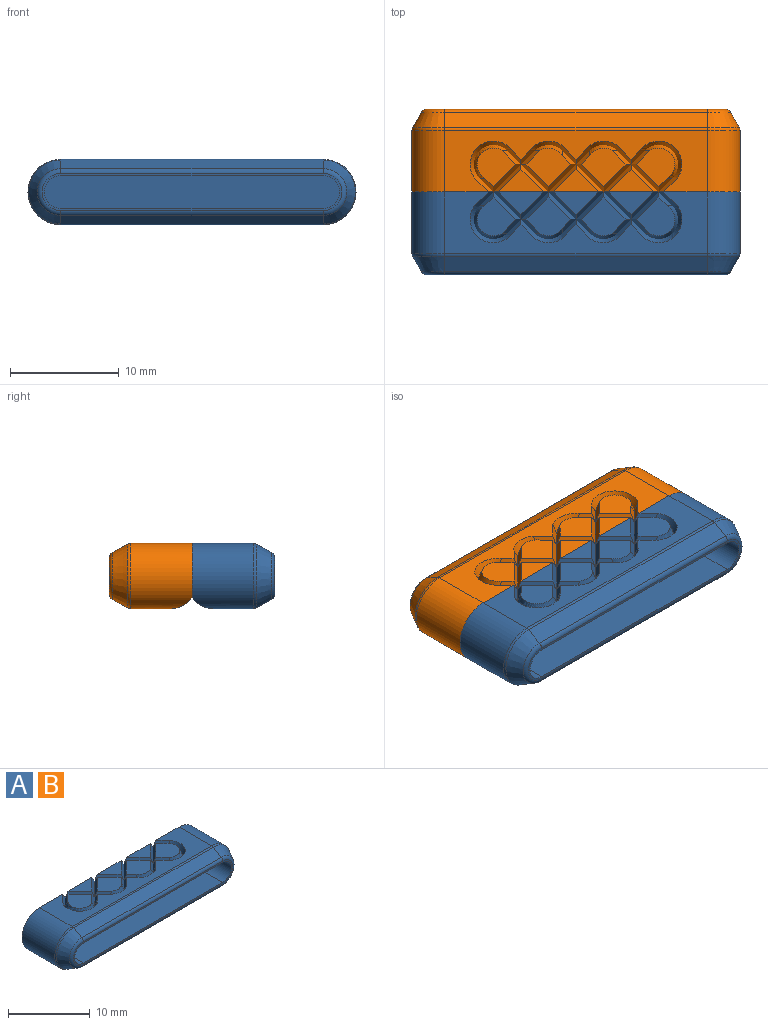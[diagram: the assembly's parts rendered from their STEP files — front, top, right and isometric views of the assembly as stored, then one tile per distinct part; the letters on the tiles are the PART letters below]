
ASSEMBLY  parts=2 mates=1
PART A: 75 faces, bbox 30.7x7.7x6.6 mm
  f0: plane 24.15x3.66mm, normal (0,0,-1), area 88.4mm2, adj f2,f3,f71,f74
  f1: plane 30.15x5mm, normal (0,1,0), area 110.2mm2, adj f2,f3,f4,f7,f16,f17,f18,f19
  f2: cylinder r=3mm len=6mm, axis (0,1,0), area 51mm2, adj f0,f1,f4,f70,f74
  f3: cylinder r=3mm len=6mm, axis (0,1,0), area 51mm2, adj f0,f1,f4,f73,f74
  f4: plane 24.22x5.73mm, normal (0,0,1), area 59.7mm2, adj f1,f2,f3,f11,f12,f14,f29,f33
  f5: plane 3.57x3.57mm, normal (0,0,1), area 7.8mm2, adj f31,f50,f52,f54
  f6: plane 4.18x3.61mm, normal (0,0,1), area 8.2mm2, adj f9,f13,f30,f47,f49
  f7: plane 4.14x2.07mm, normal (0,0,1), area 4.3mm2, adj f1,f32,f46
  f8: plane 3.57x3.57mm, normal (0,0,1), area 7.8mm2, adj f10,f34,f36,f44
  f9: plane 1.27x1.27mm, normal (-0.65,-0.65,0.38), area 1.3mm2, adj f6,f11,f30,f49
  f10: plane 1.73x1.27mm, normal (0.65,-0.65,0.38), area 1.5mm2, adj f8,f14,f36,f44
  f11: plane 1.73x1.27mm, normal (0.65,0.65,0.38), area 1.5mm2, adj f4,f9,f29,f41
  f12: plane 1.27x1.27mm, normal (-0.65,0.65,0.38), area 1.3mm2, adj f4,f13,f29,f51
  f13: plane 1.73x1.27mm, normal (0.65,-0.65,0.38), area 1.5mm2, adj f6,f12,f30,f47
  f14: plane 1.27x1.27mm, normal (-0.65,0.65,0.38), area 1.3mm2, adj f4,f10,f35,f39
  f15: plane 4.18x3.61mm, normal (0,0,1), area 8.2mm2, adj f28,f37,f38,f40,f42
  f16: plane 4.14x2.07mm, normal (0,0,1), area 4.3mm2, adj f1,f26,f48
  f17: plane 4.14x2.07mm, normal (0,0,1), area 4.3mm2, adj f1,f27,f45
  f18: cylinder r=1.65mm len=3.3mm, axis (0,-1,0), area 26.9mm2, adj f1,f25
  f19: cylinder r=1.65mm len=3.3mm, axis (0,-1,0), area 26.9mm2, adj f1,f24
  f20: cylinder r=1.65mm len=3.3mm, axis (0,-1,0), area 26.9mm2, adj f1,f23
  f21: cylinder r=1.65mm len=3.3mm, axis (0,-1,0), area 26.9mm2, adj f1,f22
  f22: plane 3.3x3.3mm, normal (0,1,0), area 8.6mm2, adj f21
  f23: plane 3.3x3.3mm, normal (0,1,0), area 8.6mm2, adj f20
  f24: plane 3.3x3.3mm, normal (0,1,0), area 8.6mm2, adj f19
  f25: plane 3.3x3.3mm, normal (0,1,0), area 8.6mm2, adj f18
  f26: plane 2.53x2.53mm, normal (-0.65,-0.65,0.38), area 2.8mm2, adj f1,f16,f28,f48
  f27: plane 2.53x2.53mm, normal (0.65,-0.65,0.38), area 2.8mm2, adj f1,f17,f37,f45
  f28: plane 2.53x2.53mm, normal (0.65,0.65,0.38), area 2.8mm2, adj f15,f26,f37,f40
  f29: bspline ~2.99x0.87mm, area 2.7mm2, adj f4,f11,f12,f30
  f30: bspline ~2.53x0.97mm, area 2.2mm2, adj f6,f9,f13,f29
  f31: plane 2.53x2.53mm, normal (-0.65,0.65,0.38), area 2.8mm2, adj f5,f32,f50,f52
  f32: plane 2.53x2.53mm, normal (0.65,-0.65,0.38), area 2.8mm2, adj f1,f7,f31,f46
  f33: plane 1.73x1.27mm, normal (0.65,-0.65,0.38), area 1.5mm2, adj f1,f4,f34,f35
  f34: plane 1.27x1.27mm, normal (-0.65,0.65,0.38), area 1.3mm2, adj f8,f33,f36,f44
  f35: bspline ~3.85x3.37mm, area 5.4mm2, adj f4,f14,f33,f36
  f36: bspline ~5.06x5.06mm, area 4.4mm2, adj f8,f10,f34,f35
  f37: plane 2.53x2.53mm, normal (-0.65,0.65,0.38), area 2.8mm2, adj f15,f27,f28,f38
  f38: plane 1.73x1.27mm, normal (-0.65,-0.65,0.38), area 1.5mm2, adj f15,f37,f39,f42
  f39: plane 1.27x1.27mm, normal (0.65,0.65,0.38), area 1.3mm2, adj f4,f14,f38,f43
  f40: plane 1.27x1.27mm, normal (0.65,-0.65,0.38), area 1.3mm2, adj f15,f28,f41,f42
  f41: plane 1.73x1.27mm, normal (-0.65,0.65,0.38), area 1.5mm2, adj f4,f11,f40,f43
  f42: bspline ~2.53x0.97mm, area 2.2mm2, adj f15,f38,f40,f43
  f43: bspline ~2.99x0.87mm, area 2.7mm2, adj f4,f39,f41,f42
  f44: plane 2.53x2.53mm, normal (0.65,0.65,0.38), area 2.8mm2, adj f8,f10,f34,f45
  f45: plane 2.53x2.53mm, normal (-0.65,-0.65,0.38), area 2.8mm2, adj f1,f17,f27,f44
  f46: plane 2.53x2.53mm, normal (-0.65,-0.65,0.38), area 2.8mm2, adj f1,f7,f32,f47
  f47: plane 2.53x2.53mm, normal (0.65,0.65,0.38), area 2.8mm2, adj f6,f13,f46,f49
  f48: plane 2.53x2.53mm, normal (0.65,-0.65,0.38), area 2.8mm2, adj f1,f16,f26,f49
  f49: plane 2.53x2.53mm, normal (-0.65,0.65,0.38), area 2.8mm2, adj f6,f9,f47,f48
  f50: plane 1.27x1.27mm, normal (0.65,0.65,0.38), area 1.3mm2, adj f5,f31,f54,f55
  f51: plane 1.27x1.27mm, normal (0.65,0.65,0.38), area 1.3mm2, adj f4,f12,f52,f53
  f52: plane 1.73x1.27mm, normal (-0.65,-0.65,0.38), area 1.5mm2, adj f5,f31,f51,f54
  f53: bspline ~3.85x3.37mm, area 5.4mm2, adj f4,f51,f54,f55
  f54: bspline ~5.06x5.06mm, area 4.4mm2, adj f5,f50,f52,f53
  f55: plane 1.73x1.27mm, normal (-0.65,-0.65,0.38), area 1.5mm2, adj f1,f4,f50,f53
  f56: cone r=2mm half-angle=29.1deg, axis (0,1,0), area 13mm2, adj f57,f59,f69,f73
  f57: plane 24.15x1.43mm, normal (0,-0.49,-0.87), area 39.5mm2, adj f56,f58,f67,f71
  f58: cone r=2mm half-angle=29.1deg, axis (0,1,0), area 13mm2, adj f57,f59,f66,f70
  f59: plane 24.15x1.43mm, normal (0,-0.49,0.87), area 39.5mm2, adj f56,f58,f68,f72
  f60: plane 27.15x3mm, normal (0,-1,0), area 79.5mm2, adj f61,f62,f63,f64
  f61: cylinder r=1.5mm len=4mm, axis (0,1,0), area 18.8mm2, adj f60,f62,f64,f65
  f62: plane 24.15x4mm, normal (0,0,1), area 96.6mm2, adj f60,f61,f63,f65
  f63: cylinder r=1.5mm len=4mm, axis (0,1,0), area 18.8mm2, adj f60,f62,f64,f65
  f64: plane 24.15x4mm, normal (0,0,-1), area 96.6mm2, adj f60,f61,f63,f65
  f65: plane 27.56x3.41mm, normal (0,-1,0), area 12mm2, adj f61,f62,f63,f64,f66,f67,f68,f69
  f66: torus R=1.71mm, axis (0,-1,0), area 3.3mm2, adj f58,f65,f67,f68
  f67: cylinder r=0.5mm len=24.15mm, axis (1,0,0), area 12.8mm2, adj f57,f65,f66,f69
  f68: cylinder r=0.5mm len=24.15mm, axis (-1,0,0), area 12.8mm2, adj f59,f65,f66,f69
  f69: torus R=1.71mm, axis (0,-1,0), area 3.3mm2, adj f56,f65,f67,f68
  f70: torus R=2.5mm, axis (0,-1,0), area 2.4mm2, adj f2,f58,f71,f72
  f71: cylinder r=0.5mm len=24.15mm, axis (1,0,0), area 6.1mm2, adj f0,f57,f70,f73
  f72: cylinder r=0.5mm len=24.15mm, axis (1,0,0), area 6.1mm2, adj f4,f59,f70,f73
  f73: torus R=2.5mm, axis (0,-1,0), area 2.4mm2, adj f3,f56,f71,f72
  f74: cylinder r=2.5mm len=28.62mm, axis (1,0,0), area 61.5mm2, adj f0,f1,f2,f3
PART B: same geometry as A
PLACE A t=(0,-15.86,0)mm
PLACE B rot(axis=(0,0,1),180deg) t=(0,-8.68,0)mm
MATE fastened B.f2 <-> A.f19  axis (0,-1,0) through (-12.08,-12.27,0)mm
